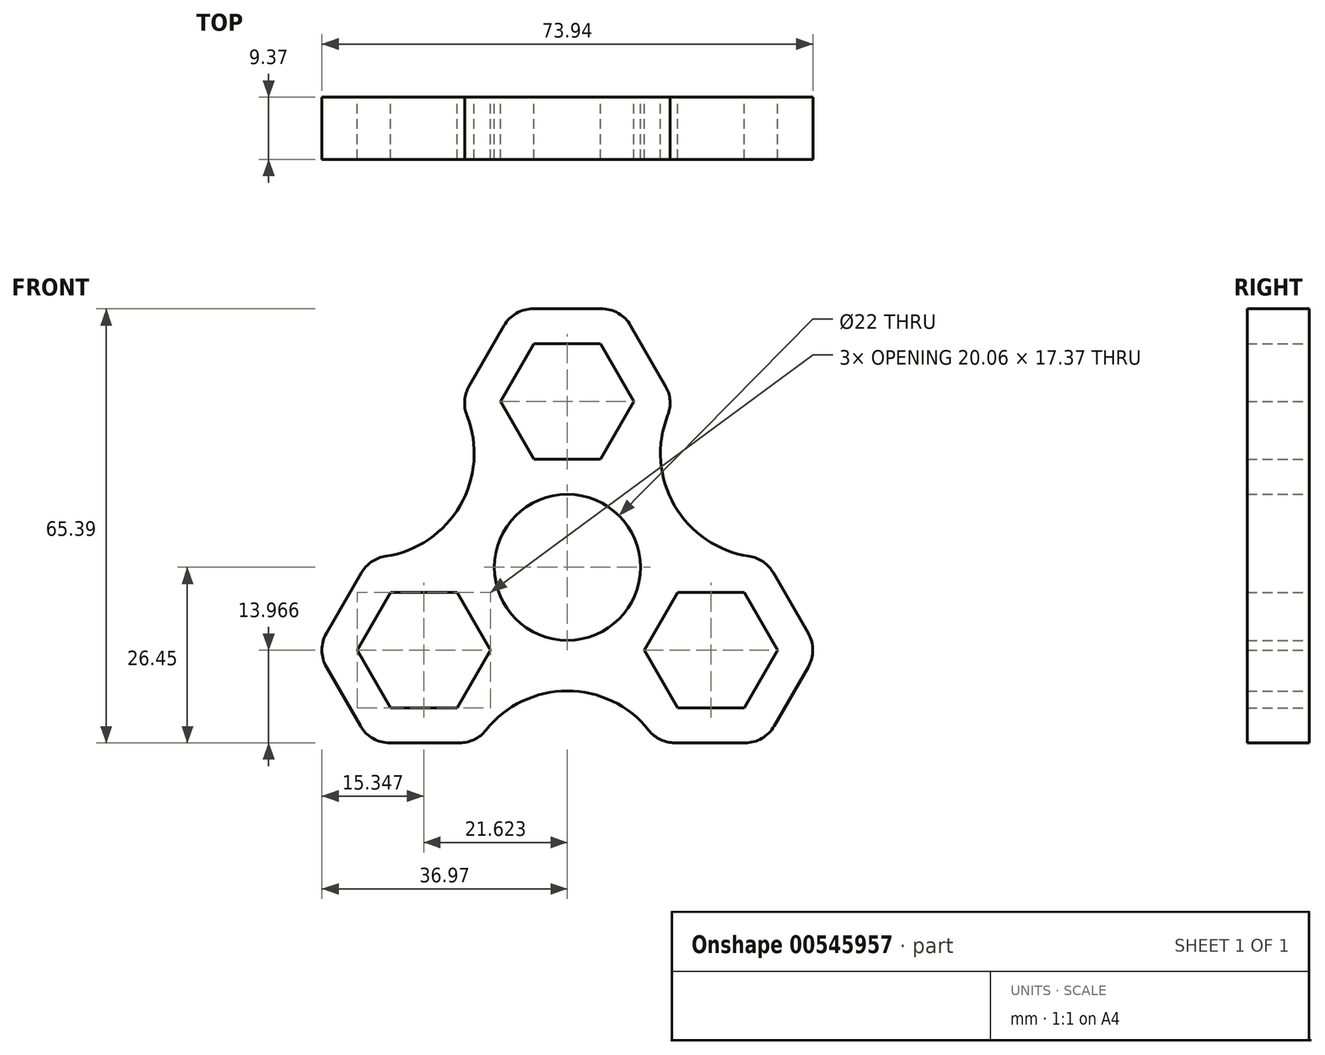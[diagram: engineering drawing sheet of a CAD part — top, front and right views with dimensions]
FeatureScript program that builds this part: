
annotation { "Feature Type Name" : "Feature", "Feature Type Description" : "" }
export const myFeature = defineFeature(function(context is Context, id is Id, definition is map)
    precondition{}
    {
        {
            var Q0;
            Q0=qCreatedBy(makeId("Front.planeOp"),FACE);
            var sketch = newSketch(context, id + "F0", { "sketchPlane" : qUnion([Q0])});
            skCircle(sketch, "E0", {"center": v(0, 0) * mm, "radius": 11 * mm});
            skCircle(sketch, "E1.cCircle", {"center": v(0, 0) * mm, "radius": 16.64 * mm, "construction": true});
            skLineSegment(sketch, "E1.0", {"start": v(-9.6, 16.64) * mm, "end": v(9.6, 16.64) * mm});
            skLineSegment(sketch, "E1.1", {"start": v(9.6, 16.64) * mm, "end": v(19.21, 0) * mm});
            skLineSegment(sketch, "E1.2", {"start": v(19.21, 0) * mm, "end": v(9.6, -16.64) * mm});
            skLineSegment(sketch, "E1.3", {"start": v(9.6, -16.64) * mm, "end": v(-9.6, -16.64) * mm});
            skLineSegment(sketch, "E1.4", {"start": v(-9.6, -16.64) * mm, "end": v(-19.21, 0) * mm});
            skLineSegment(sketch, "E1.5", {"start": v(-19.21, 0) * mm, "end": v(-9.6, 16.64) * mm});
            skPoint(sketch, "E1.0.midPoint", {"position": v(0, 16.64) * mm});
            skCircle(sketch, "E2.cCircle", {"center": v(0, 24.97) * mm, "radius": 13.97 * mm, "construction": true});
            skLineSegment(sketch, "E2.0", {"start": v(8.07, 11) * mm, "end": v(-8.07, 11) * mm});
            skLineSegment(sketch, "E2.1", {"start": v(-8.07, 11) * mm, "end": v(-16.13, 24.97) * mm});
            skLineSegment(sketch, "E2.2", {"start": v(-16.13, 24.97) * mm, "end": v(-8.07, 38.94) * mm});
            skLineSegment(sketch, "E2.3", {"start": v(-8.07, 38.94) * mm, "end": v(8.07, 38.94) * mm});
            skLineSegment(sketch, "E2.4", {"start": v(8.07, 38.94) * mm, "end": v(16.13, 24.97) * mm});
            skLineSegment(sketch, "E2.5", {"start": v(16.13, 24.97) * mm, "end": v(8.07, 11) * mm});
            skPoint(sketch, "E2.0.midPoint", {"position": v(0, 11) * mm});
            skCircle(sketch, "E3.cCircle", {"center": v(0, 24.97) * mm, "radius": 8.69 * mm, "construction": true});
            skLineSegment(sketch, "E3.0", {"start": v(-5.02, 33.66) * mm, "end": v(5.02, 33.66) * mm});
            skLineSegment(sketch, "E3.1", {"start": v(5.02, 33.66) * mm, "end": v(10.03, 24.97) * mm});
            skLineSegment(sketch, "E3.2", {"start": v(10.03, 24.97) * mm, "end": v(5.02, 16.28) * mm});
            skLineSegment(sketch, "E3.3", {"start": v(5.02, 16.28) * mm, "end": v(-5.02, 16.28) * mm});
            skLineSegment(sketch, "E3.4", {"start": v(-5.02, 16.28) * mm, "end": v(-10.03, 24.97) * mm});
            skLineSegment(sketch, "E3.5", {"start": v(-10.03, 24.97) * mm, "end": v(-5.02, 33.66) * mm});
            skPoint(sketch, "E3.0.midPoint", {"position": v(0, 33.66) * mm});
            skLineSegment(sketch, "E4.1.0", {"start": v(-29.69, -26.45) * mm, "end": v(-37.75, -12.48) * mm});
            skLineSegment(sketch, "E4.1.1", {"start": v(-13.56, -26.45) * mm, "end": v(-29.69, -26.45) * mm});
            skCircle(sketch, "E4.1.2", {"center": v(-21.62, -12.48) * mm, "radius": 13.97 * mm, "construction": true});
            skCircle(sketch, "E4.1.3", {"center": v(-21.62, -12.48) * mm, "radius": 8.69 * mm, "construction": true});
            skLineSegment(sketch, "E4.1.4", {"start": v(-5.5, -12.48) * mm, "end": v(-13.56, -26.45) * mm});
            skLineSegment(sketch, "E4.1.5", {"start": v(-13.56, 1.49) * mm, "end": v(-5.5, -12.48) * mm});
            skLineSegment(sketch, "E4.1.6", {"start": v(-29.69, 1.49) * mm, "end": v(-13.56, 1.49) * mm});
            skLineSegment(sketch, "E4.1.7", {"start": v(-37.75, -12.48) * mm, "end": v(-29.69, 1.49) * mm});
            skLineSegment(sketch, "E4.1.8", {"start": v(-26.64, -21.17) * mm, "end": v(-31.65, -12.48) * mm});
            skLineSegment(sketch, "E4.1.9", {"start": v(-31.65, -12.48) * mm, "end": v(-26.64, -3.8) * mm});
            skLineSegment(sketch, "E4.1.10", {"start": v(-16.6, -21.17) * mm, "end": v(-26.64, -21.17) * mm});
            skLineSegment(sketch, "E4.1.11", {"start": v(-11.6, -12.48) * mm, "end": v(-16.6, -21.17) * mm});
            skLineSegment(sketch, "E4.1.12", {"start": v(-16.6, -3.8) * mm, "end": v(-11.6, -12.48) * mm});
            skLineSegment(sketch, "E4.1.13", {"start": v(-26.64, -3.8) * mm, "end": v(-16.6, -3.8) * mm});
            skLineSegment(sketch, "E4.2.0", {"start": v(37.75, -12.48) * mm, "end": v(29.69, -26.45) * mm});
            skLineSegment(sketch, "E4.2.1", {"start": v(29.69, 1.49) * mm, "end": v(37.75, -12.48) * mm});
            skCircle(sketch, "E4.2.2", {"center": v(21.62, -12.48) * mm, "radius": 13.97 * mm, "construction": true});
            skCircle(sketch, "E4.2.3", {"center": v(21.62, -12.48) * mm, "radius": 8.69 * mm, "construction": true});
            skLineSegment(sketch, "E4.2.4", {"start": v(13.56, 1.49) * mm, "end": v(29.69, 1.49) * mm});
            skLineSegment(sketch, "E4.2.5", {"start": v(5.5, -12.48) * mm, "end": v(13.56, 1.49) * mm});
            skLineSegment(sketch, "E4.2.6", {"start": v(13.56, -26.45) * mm, "end": v(5.5, -12.48) * mm});
            skLineSegment(sketch, "E4.2.7", {"start": v(29.69, -26.45) * mm, "end": v(13.56, -26.45) * mm});
            skLineSegment(sketch, "E4.2.8", {"start": v(31.65, -12.48) * mm, "end": v(26.64, -21.17) * mm});
            skLineSegment(sketch, "E4.2.9", {"start": v(26.64, -21.17) * mm, "end": v(16.6, -21.17) * mm});
            skLineSegment(sketch, "E4.2.10", {"start": v(26.64, -3.8) * mm, "end": v(31.65, -12.48) * mm});
            skLineSegment(sketch, "E4.2.11", {"start": v(16.6, -3.8) * mm, "end": v(26.64, -3.8) * mm});
            skLineSegment(sketch, "E4.2.12", {"start": v(11.6, -12.48) * mm, "end": v(16.6, -3.8) * mm});
            skLineSegment(sketch, "E4.2.13", {"start": v(16.6, -21.17) * mm, "end": v(11.6, -12.48) * mm});
            skArc(sketch, "E5", {"start": v(16.13, 24.97) * mm, "mid": v(16.13, 9.31) * mm, "end": v(29.69, 1.49) * mm});
            skArc(sketch, "E6", {"start": v(13.56, -26.45) * mm, "mid": v(0, -18.63) * mm, "end": v(-13.56, -26.45) * mm});
            skArc(sketch, "E7", {"start": v(-29.69, 1.49) * mm, "mid": v(-16.13, 9.31) * mm, "end": v(-16.13, 24.97) * mm});
            skSolve(sketch);
        }
        {
            var Q0;
            Q0 = qSketchRegion(id + "F0", true);
            var Q1;
            {var subQ0=sQuery(id+"F0.wireOp",EDGE,"E4.1.12");Q1=makeQuery(id+"F0.imprint","IMPRINT",FACE,{"disambiguationData":[TD([[makeQuery(id+"F0.imprint","IMPRINT",EDGE,{"derivedFrom":subQ0}),1.0]])]});}
            var Q2;
            {var subQ0=sQuery(id+"F0.wireOp",EDGE,"E4.1.5");var subQ9=sQuery(id+"F0.wireOp",EDGE,"E0");var subQ10=makeQuery(id+"F0.imprint","INTERSECT",VERTEX,{"derivedFrom":[subQ9,subQ0]});Q2=makeQuery(id+"F0.imprint","IMPRINT",FACE,{"disambiguationData":[TD([[makeQuery(id+"F0.imprint","IMPRINT",EDGE,{"disambiguationData":[TD([[subQ10,-1.0]])],"derivedFrom":subQ9}),-1.0]])]});}
            var Q3;
            {var subQ0=sQuery(id+"F0.wireOp",EDGE,"E4.2.12");Q3=makeQuery(id+"F0.imprint","IMPRINT",FACE,{"disambiguationData":[TD([[makeQuery(id+"F0.imprint","IMPRINT",EDGE,{"derivedFrom":subQ0}),1.0]])]});}
            var Q4;
            {var subQ1=sQuery(id+"F0.wireOp",EDGE,"E2.0");var subQ7=sQuery(id+"F0.wireOp",EDGE,"E0");var subQ8=makeQuery(id+"F0.imprint","INTERSECT",VERTEX,{"derivedFrom":[subQ7,subQ1]});Q4=makeQuery(id+"F0.imprint","IMPRINT",FACE,{"disambiguationData":[TD([[makeQuery(id+"F0.imprint","IMPRINT",EDGE,{"disambiguationData":[TD([[subQ8,1.0]])],"derivedFrom":subQ7}),-1.0]])]});}
            var Q5;
            {var subQ6=sQuery(id+"F0.wireOp",EDGE,"E4.1.5");var subQ9=sQuery(id+"F0.wireOp",EDGE,"E0");var subQ11=makeQuery(id+"F0.imprint","INTERSECT",VERTEX,{"derivedFrom":[subQ9,subQ6]});Q5=makeQuery(id+"F0.imprint","IMPRINT",FACE,{"disambiguationData":[TD([[makeQuery(id+"F0.imprint","IMPRINT",EDGE,{"disambiguationData":[TD([[subQ11,1.0]])],"derivedFrom":subQ9}),-1.0]])]});}
            var Q6;
            {var subQ7=sQuery(id+"F0.wireOp",EDGE,"E3.3");Q6=makeQuery(id+"F0.imprint","IMPRINT",FACE,{"disambiguationData":[TD([[makeQuery(id+"F0.imprint","IMPRINT",EDGE,{"derivedFrom":subQ7}),1.0]])]});}
            extrude(context, id + "F1", {"entities" : qUnion([Q0, Q1, Q2, Q3, Q4, Q5, Q6]), "depth" : 9.37 * mm, "offsetDistance" : 25.4 * mm});
        }
        {
            var Q0;
            Q0=makeQuery(id+"F1.opExtrude","SWEPT_EDGE",EDGE,{"disambiguationData":[OSD([sQuery(id+"F0.wireOp",EDGE,"E2.3"),sQuery(id+"F0.wireOp",EDGE,"E2.4")])]});
            var Q1;
            Q1=makeQuery(id+"F1.opExtrude","SWEPT_EDGE",EDGE,{"disambiguationData":[OSD([sQuery(id+"F0.wireOp",EDGE,"E2.4"),sQuery(id+"F0.wireOp",EDGE,"E2.5"),sQuery(id+"F0.wireOp",EDGE,"E5")])]});
            var Q2;
            Q2=makeQuery(id+"F1.opExtrude","SWEPT_EDGE",EDGE,{"disambiguationData":[OSD([sQuery(id+"F0.wireOp",EDGE,"E2.2"),sQuery(id+"F0.wireOp",EDGE,"E2.3")])]});
            var Q3;
            Q3=makeQuery(id+"F1.opExtrude","SWEPT_EDGE",EDGE,{"disambiguationData":[OSD([sQuery(id+"F0.wireOp",EDGE,"E2.1"),sQuery(id+"F0.wireOp",EDGE,"E2.2"),sQuery(id+"F0.wireOp",EDGE,"E7")])]});
            var Q4;
            Q4=makeQuery(id+"F1.opExtrude","SWEPT_EDGE",EDGE,{"disambiguationData":[OSD([sQuery(id+"F0.wireOp",EDGE,"E4.1.6"),sQuery(id+"F0.wireOp",EDGE,"E4.1.7"),sQuery(id+"F0.wireOp",EDGE,"E7")])]});
            var Q5;
            Q5=makeQuery(id+"F1.opExtrude","SWEPT_EDGE",EDGE,{"disambiguationData":[OSD([sQuery(id+"F0.wireOp",EDGE,"E4.1.0"),sQuery(id+"F0.wireOp",EDGE,"E4.1.7")])]});
            var Q6;
            Q6=makeQuery(id+"F1.opExtrude","SWEPT_EDGE",EDGE,{"disambiguationData":[OSD([sQuery(id+"F0.wireOp",EDGE,"E4.1.0"),sQuery(id+"F0.wireOp",EDGE,"E4.1.1")])]});
            var Q7;
            Q7=makeQuery(id+"F1.opExtrude","SWEPT_EDGE",EDGE,{"disambiguationData":[OSD([sQuery(id+"F0.wireOp",EDGE,"E4.1.1"),sQuery(id+"F0.wireOp",EDGE,"E4.1.4"),sQuery(id+"F0.wireOp",EDGE,"E6")])]});
            var Q8;
            Q8=makeQuery(id+"F1.opExtrude","SWEPT_EDGE",EDGE,{"disambiguationData":[OSD([sQuery(id+"F0.wireOp",EDGE,"E4.2.6"),sQuery(id+"F0.wireOp",EDGE,"E4.2.7"),sQuery(id+"F0.wireOp",EDGE,"E6")])]});
            var Q9;
            Q9=makeQuery(id+"F1.opExtrude","SWEPT_EDGE",EDGE,{"disambiguationData":[OSD([sQuery(id+"F0.wireOp",EDGE,"E4.2.0"),sQuery(id+"F0.wireOp",EDGE,"E4.2.7")])]});
            var Q10;
            Q10=makeQuery(id+"F1.opExtrude","SWEPT_EDGE",EDGE,{"disambiguationData":[OSD([sQuery(id+"F0.wireOp",EDGE,"E4.2.0"),sQuery(id+"F0.wireOp",EDGE,"E4.2.1")])]});
            var Q11;
            Q11=makeQuery(id+"F1.opExtrude","SWEPT_EDGE",EDGE,{"disambiguationData":[OSD([sQuery(id+"F0.wireOp",EDGE,"E4.2.1"),sQuery(id+"F0.wireOp",EDGE,"E4.2.4"),sQuery(id+"F0.wireOp",EDGE,"E5")])]});
            fillet(context, id + "F2", {"entities" : qUnion([Q0, Q1, Q2, Q3, Q4, Q5, Q6, Q7, Q8, Q9, Q10, Q11]), "radius" : 5.08 * mm, "tangentPropagation" : true, "allowEdgeOverflow" : false});
        }
    });
